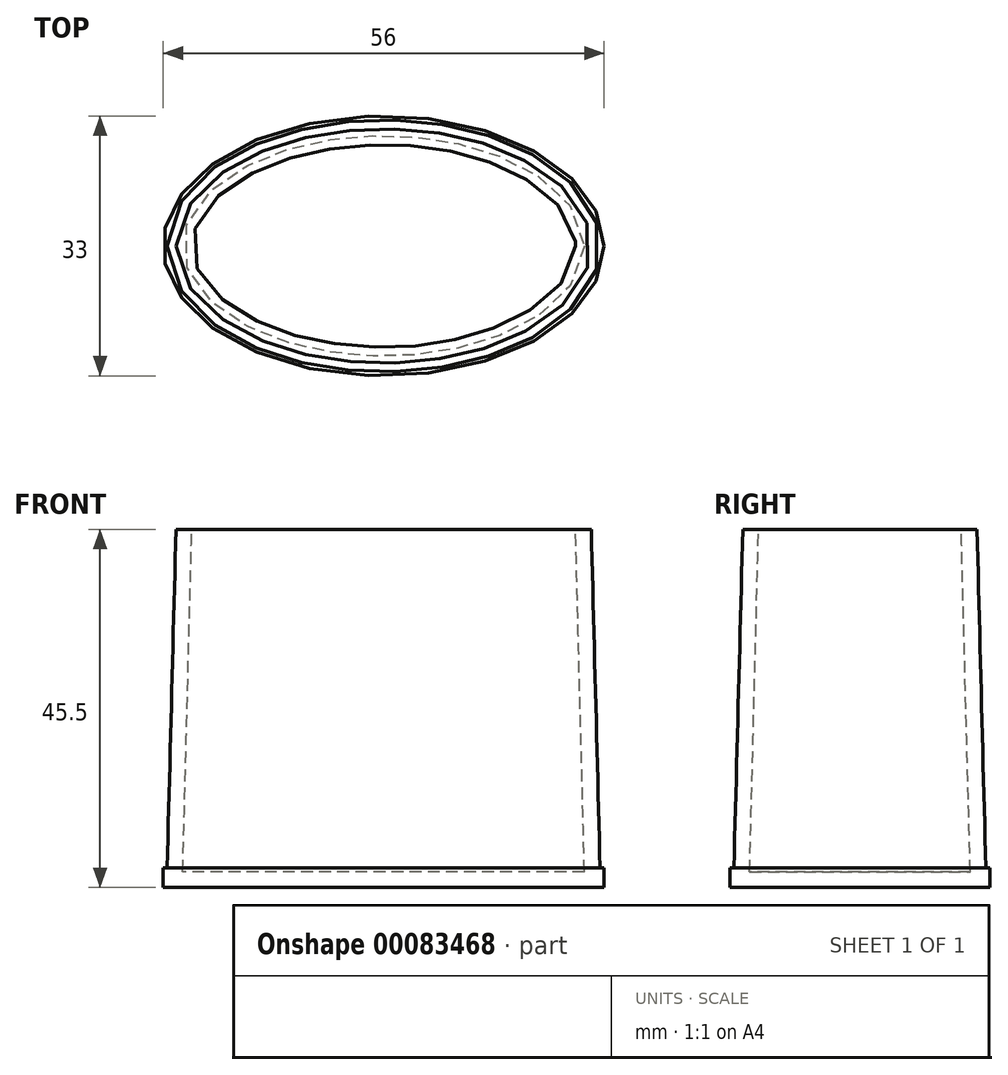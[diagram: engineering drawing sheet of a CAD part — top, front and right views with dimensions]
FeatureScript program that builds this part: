
annotation { "Feature Type Name" : "Feature", "Feature Type Description" : "" }
export const myFeature = defineFeature(function(context is Context, id is Id, definition is map)
    precondition{}
    {
        {
            var Q0;
            Q0=qCreatedBy(makeId("Top.planeOp"),FACE);
            var sketch = newSketch(context, id + "F0", { "sketchPlane" : qUnion([Q0])});
            skEllipse(sketch, "E0", {"center": v(0, 0) * mm, "majorRadius": 27.5 * mm, "minorRadius": 16 * mm, "majorAxis": v(1, 0)});
            skSolve(sketch);
        }
        {
            var Q0;
            Q0=makeQuery(id+"F0.imprint","IMPRINT",FACE,{"disambiguationData":[TD([[makeQuery(id+"F0.imprint","IMPRINT",EDGE,{"derivedFrom":sQuery(id+"F0.wireOp",EDGE,"E0")}),1.0]])]});
            extrude(context, id + "F1", {"entities" : qUnion([Q0]), "depth" : 43 * mm, "hasDraft" : true, "draftAngle" : 1.5 * degree, "draftPullDirection" : true});
        }
        {
            var Q0;
            Q0=qCreatedBy(makeId("Top.planeOp"),FACE);
            var sketch = newSketch(context, id + "F2", { "sketchPlane" : qUnion([Q0])});
            skEllipse(sketch, "E1", {"center": v(0, 0) * mm, "majorRadius": 28 * mm, "minorRadius": 16.5 * mm, "majorAxis": v(1, 0)});
            skSolve(sketch);
        }
        {
            var Q0;
            Q0=makeQuery(id+"F2.imprint","IMPRINT",FACE,{"disambiguationData":[TD([[makeQuery(id+"F2.imprint","IMPRINT",EDGE,{"derivedFrom":sQuery(id+"F2.wireOp",EDGE,"E1")}),1.0]])]});
            extrude(context, id + "F3", {"entities" : qUnion([Q0]), "operationType" : NewBodyOperationType.ADD, "oppositeDirection" : true, "depth" : 2.5 * mm});
        }
        {
            var Q0;
            Q0=makeQuery(id+"F1.opExtrude","CAP_FACE",FACE,{"disambiguationData":[OSD([sQuery(id+"F0.wireOp",EDGE,"E0")])],"isStart":false});
            shell(context, id + "F4", {"entities" : qUnion([Q0]), "thickness" : 2 * mm});
        }
    });
